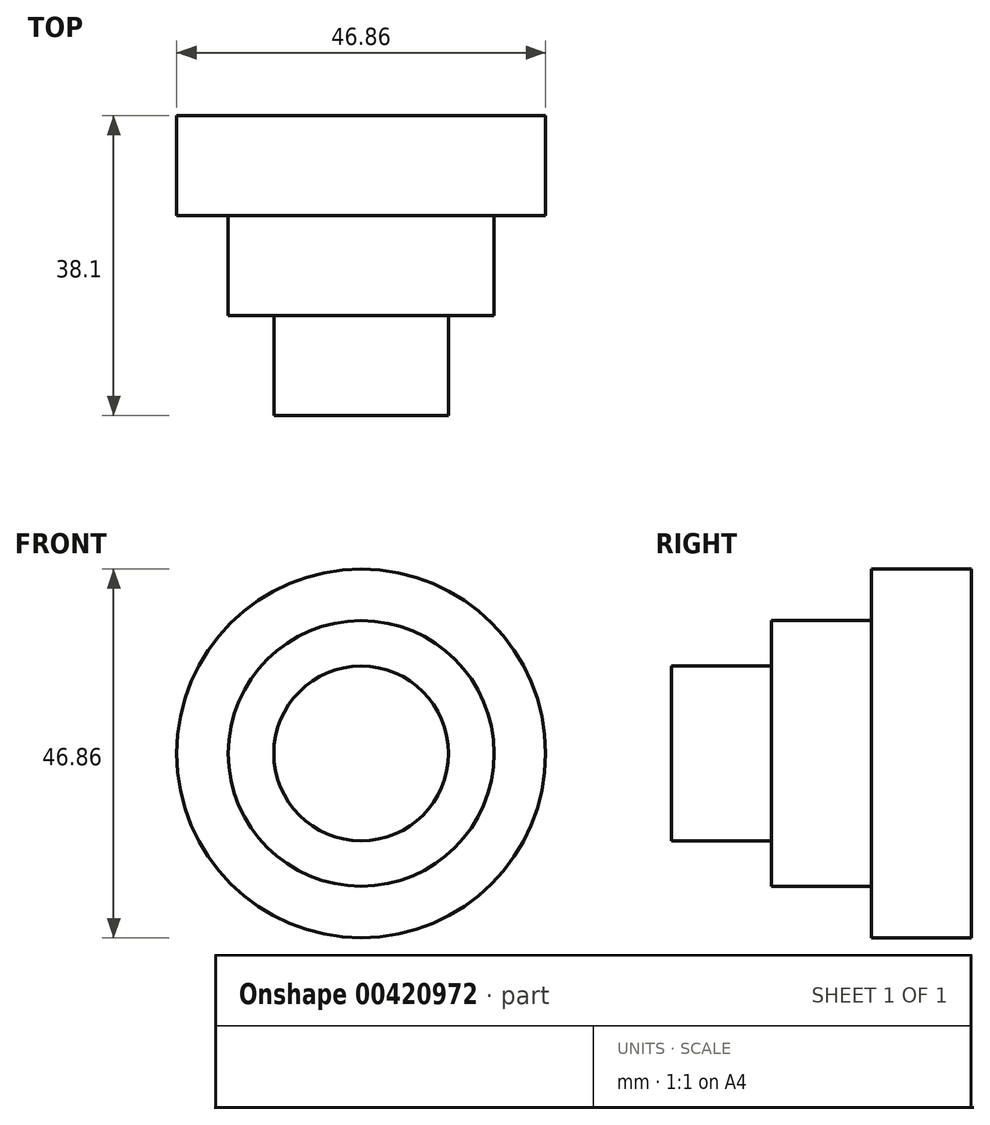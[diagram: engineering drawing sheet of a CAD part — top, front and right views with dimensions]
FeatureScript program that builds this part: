
annotation { "Feature Type Name" : "Feature", "Feature Type Description" : "" }
export const myFeature = defineFeature(function(context is Context, id is Id, definition is map)
    precondition{}
    {
        {
            var Q0;
            Q0=qCreatedBy(makeId("Front.planeOp"),FACE);
            var sketch = newSketch(context, id + "F0", { "sketchPlane" : qUnion([Q0])});
            skCircle(sketch, "E0", {"center": v(0, 6.86) * mm, "radius": 23.43 * mm});
            skSolve(sketch);
        }
        {
            var Q0;
            Q0=makeQuery(id+"F0.imprint","IMPRINT",FACE,{"disambiguationData":[TD([[makeQuery(id+"F0.imprint","IMPRINT",EDGE,{"derivedFrom":sQuery(id+"F0.wireOp",EDGE,"E0")}),1.0]])]});
            extrude(context, id + "F1", {"entities" : qUnion([Q0]), "depth" : 12.7 * mm});
        }
        {
            var Q0;
            Q0=makeQuery(id+"F1.opExtrude","CAP_FACE",FACE,{"disambiguationData":[OSD([sQuery(id+"F0.wireOp",EDGE,"E0")])],"isStart":false});
            var sketch = newSketch(context, id + "F2", { "sketchPlane" : qUnion([Q0])});
            skCircle(sketch, "E1", {"center": v(0, 6.86) * mm, "radius": 16.88 * mm});
            skSolve(sketch);
        }
        {
            var Q0;
            Q0 = qSketchRegion(id + "F2", true);
            extrude(context, id + "F3", {"entities" : qUnion([Q0]), "operationType" : NewBodyOperationType.ADD, "depth" : 12.7 * mm});
        }
        {
            var Q0;
            Q0=makeQuery(id+"F3.opExtrude","CAP_FACE",FACE,{"disambiguationData":[OSD([sQuery(id+"F2.wireOp",EDGE,"E1")])],"isStart":false});
            var sketch = newSketch(context, id + "F4", { "sketchPlane" : qUnion([Q0])});
            skCircle(sketch, "E2", {"center": v(0, 6.86) * mm, "radius": 11.1 * mm});
            skSolve(sketch);
        }
        {
            var Q0;
            Q0=makeQuery(id+"F4.imprint","IMPRINT",FACE,{"disambiguationData":[TD([[makeQuery(id+"F4.imprint","IMPRINT",EDGE,{"derivedFrom":sQuery(id+"F4.wireOp",EDGE,"E2")}),1.0]])]});
            extrude(context, id + "F5", {"entities" : qUnion([Q0]), "operationType" : NewBodyOperationType.ADD, "depth" : 12.7 * mm});
        }
    });
